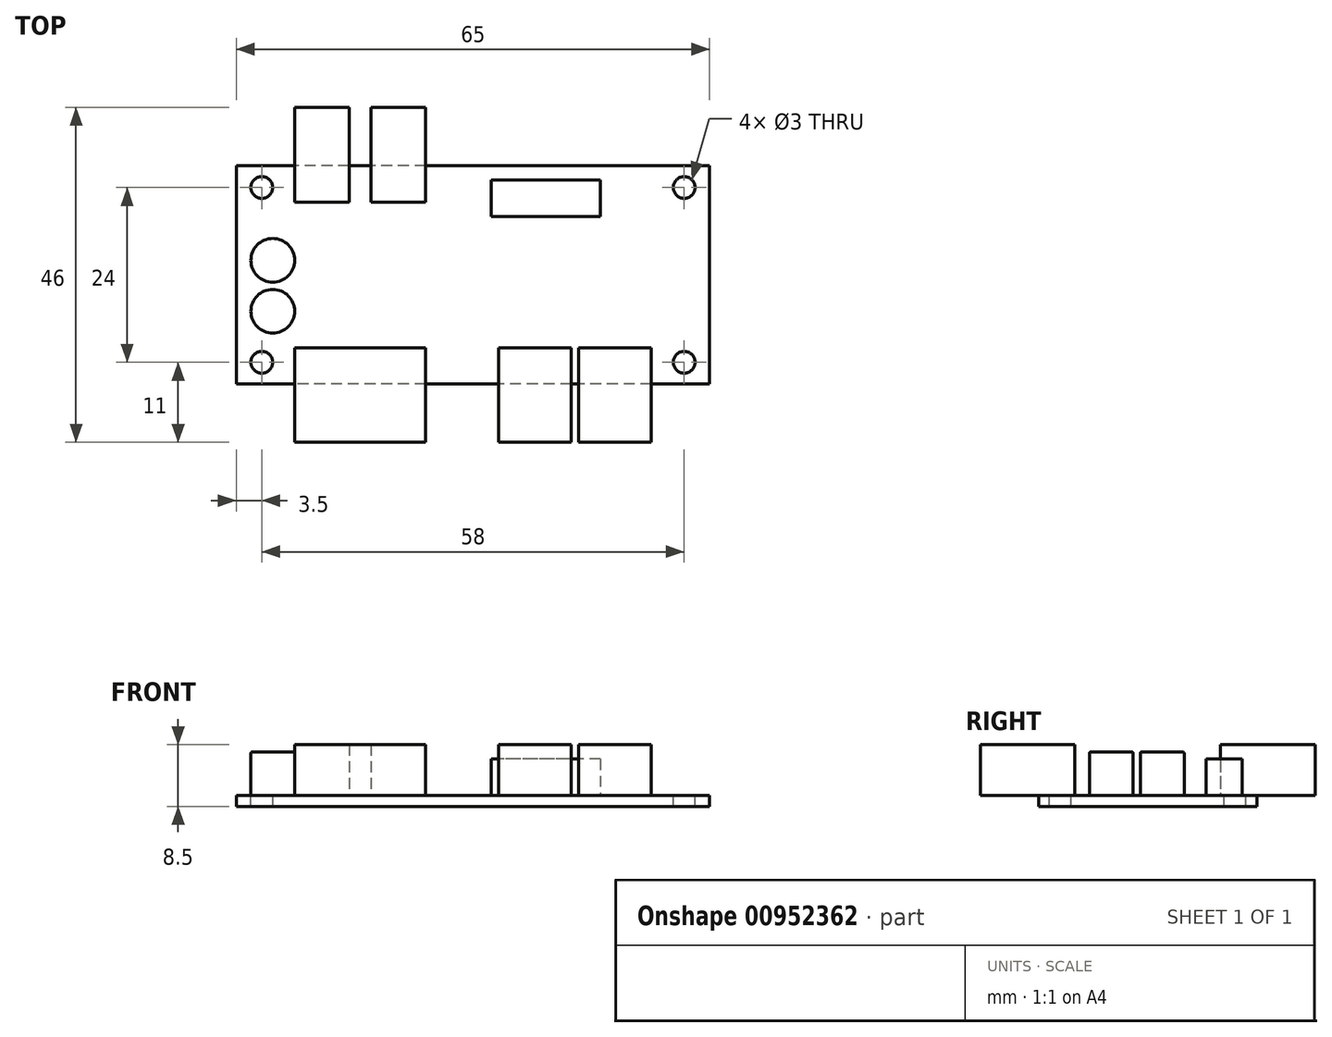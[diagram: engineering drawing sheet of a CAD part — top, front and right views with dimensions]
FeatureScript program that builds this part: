
annotation { "Feature Type Name" : "Feature", "Feature Type Description" : "" }
export const myFeature = defineFeature(function(context is Context, id is Id, definition is map)
    precondition{}
    {
        {
            var Q0;
            Q0=qCreatedBy(makeId("Top.planeOp"),FACE);
            var sketch = newSketch(context, id + "F0", { "sketchPlane" : qUnion([Q0])});
            skLineSegment(sketch, "E0.bottom", {"start": v(32.5, 15) * mm, "end": v(-32.5, 15) * mm});
            skLineSegment(sketch, "E0.top", {"start": v(32.5, -15) * mm, "end": v(-32.5, -15) * mm});
            skLineSegment(sketch, "E0.left", {"start": v(32.5, 15) * mm, "end": v(32.5, -15) * mm});
            skLineSegment(sketch, "E0.right", {"start": v(-32.5, 15) * mm, "end": v(-32.5, -15) * mm});
            skPoint(sketch, "E0.middle", {"position": v(0, 0) * mm});
            skSolve(sketch);
        }
        {
            var Q0;
            Q0 = qSketchRegion(id + "F0", true);
            extrude(context, id + "F1", {"entities" : qUnion([Q0]), "depth" : 1.5 * mm, "offsetDistance" : 25 * mm});
        }
        {
            var Q0;
            Q0=makeQuery(id+"F1.opExtrude","CAP_FACE",FACE,{"disambiguationData":[OSD([sQuery(id+"F0.wireOp",EDGE,"E0.bottom"),sQuery(id+"F0.wireOp",EDGE,"E0.top"),sQuery(id+"F0.wireOp",EDGE,"E0.left"),sQuery(id+"F0.wireOp",EDGE,"E0.right")])],"isStart":false});
            var sketch = newSketch(context, id + "F2", { "sketchPlane" : qUnion([Q0])});
            skCircle(sketch, "E1", {"center": v(-29, 12) * mm, "radius": 1.5 * mm});
            skCircle(sketch, "E2.0.1.0", {"center": v(-29, -12) * mm, "radius": 1.5 * mm});
            skCircle(sketch, "E2.1.0.0", {"center": v(29, 12) * mm, "radius": 1.5 * mm});
            skCircle(sketch, "E2.1.1.0", {"center": v(29, -12) * mm, "radius": 1.5 * mm});
            skLineSegment(sketch, "E2.direction1", {"start": v(-29, 12) * mm, "end": v(29, 12) * mm, "construction": true});
            skLineSegment(sketch, "E2.direction2", {"start": v(-29, 12) * mm, "end": v(-29, -12) * mm, "construction": true});
            skSolve(sketch);
        }
        {
            var Q0;
            Q0 = qSketchRegion(id + "F2", true);
            extrude(context, id + "F3", {"entities" : qUnion([Q0]), "operationType" : NewBodyOperationType.REMOVE, "endBound" : BoundingType.THROUGH_ALL, "oppositeDirection" : true, "depth" : 25 * mm, "offsetDistance" : 25 * mm});
        }
        {
            var Q0;
            Q0=makeQuery(id+"F1.opExtrude","CAP_FACE",FACE,{"disambiguationData":[OSD([sQuery(id+"F0.wireOp",EDGE,"E0.bottom"),sQuery(id+"F0.wireOp",EDGE,"E0.top"),sQuery(id+"F0.wireOp",EDGE,"E0.left"),sQuery(id+"F0.wireOp",EDGE,"E0.right")])],"isStart":false});
            var sketch = newSketch(context, id + "F4", { "sketchPlane" : qUnion([Q0])});
            skCircle(sketch, "E3", {"center": v(-27.5, 2) * mm, "radius": 3 * mm});
            skCircle(sketch, "E4", {"center": v(-27.5, -5) * mm, "radius": 3 * mm});
            skSolve(sketch);
        }
        {
            var Q0;
            Q0 = qSketchRegion(id + "F4", true);
            extrude(context, id + "F5", {"entities" : qUnion([Q0]), "operationType" : NewBodyOperationType.ADD, "depth" : 6 * mm, "offsetDistance" : 25 * mm});
        }
        {
            var Q0;
            Q0=makeQuery(id+"F5.opExtrude","CAP_EDGE",EDGE,{"disambiguationData":[OSD([sQuery(id+"F4.wireOp",EDGE,"E3")])],"isStart":false});
            var Q1;
            Q1=makeQuery(id+"F5.opExtrude","CAP_EDGE",EDGE,{"disambiguationData":[OSD([sQuery(id+"F4.wireOp",EDGE,"E4")])],"isStart":false});
            fillet(context, id + "F6", {"entities" : qUnion([Q0, Q1]), "radius" : 0.2 * mm, "tangentPropagation" : true, "allowEdgeOverflow" : false});
        }
        {
            var Q0;
            Q0=makeQuery(id+"F1.opExtrude","CAP_FACE",FACE,{"disambiguationData":[OSD([sQuery(id+"F0.wireOp",EDGE,"E0.bottom"),sQuery(id+"F0.wireOp",EDGE,"E0.top"),sQuery(id+"F0.wireOp",EDGE,"E0.left"),sQuery(id+"F0.wireOp",EDGE,"E0.right")])],"isStart":false});
            var sketch = newSketch(context, id + "F7", { "sketchPlane" : qUnion([Q0])});
            skLineSegment(sketch, "E5.bottom", {"start": v(-17, 23) * mm, "end": v(-24.5, 23) * mm});
            skLineSegment(sketch, "E5.top", {"start": v(-17, 10) * mm, "end": v(-24.5, 10) * mm});
            skLineSegment(sketch, "E5.left", {"start": v(-17, 23) * mm, "end": v(-17, 10) * mm});
            skLineSegment(sketch, "E5.right", {"start": v(-24.5, 23) * mm, "end": v(-24.5, 10) * mm});
            skPoint(sketch, "E5.middle", {"position": v(-20.75, 16.5) * mm});
            skLineSegment(sketch, "E6.1.0.0", {"start": v(-6.5, 10) * mm, "end": v(-14, 10) * mm});
            skLineSegment(sketch, "E6.1.0.1", {"start": v(-14, 23) * mm, "end": v(-14, 10) * mm});
            skLineSegment(sketch, "E6.1.0.2", {"start": v(-6.5, 23) * mm, "end": v(-6.5, 10) * mm});
            skPoint(sketch, "E6.1.0.3", {"position": v(-10.25, 16.5) * mm});
            skLineSegment(sketch, "E6.1.0.4", {"start": v(-6.5, 23) * mm, "end": v(-14, 23) * mm});
            skLineSegment(sketch, "E6.direction1", {"start": v(-24.5, 10) * mm, "end": v(-14, 10) * mm, "construction": true});
            skLineSegment(sketch, "E7.bottom", {"start": v(-6.5, -23) * mm, "end": v(-24.5, -23) * mm});
            skLineSegment(sketch, "E7.top", {"start": v(-6.5, -10) * mm, "end": v(-24.5, -10) * mm});
            skLineSegment(sketch, "E7.left", {"start": v(-6.5, -23) * mm, "end": v(-6.5, -10) * mm});
            skLineSegment(sketch, "E7.right", {"start": v(-24.5, -23) * mm, "end": v(-24.5, -10) * mm});
            skPoint(sketch, "E7.middle", {"position": v(-15.5, -16.5) * mm});
            skLineSegment(sketch, "E8.bottom", {"start": v(24.5, -10) * mm, "end": v(14.5, -10) * mm});
            skLineSegment(sketch, "E8.top", {"start": v(24.5, -23) * mm, "end": v(14.5, -23) * mm});
            skLineSegment(sketch, "E8.left", {"start": v(24.5, -10) * mm, "end": v(24.5, -23) * mm});
            skLineSegment(sketch, "E8.right", {"start": v(14.5, -10) * mm, "end": v(14.5, -23) * mm});
            skPoint(sketch, "E8.middle", {"position": v(19.5, -16.5) * mm});
            skLineSegment(sketch, "E9.1.0.0", {"start": v(13.5, -10) * mm, "end": v(3.5, -10) * mm});
            skPoint(sketch, "E9.1.0.1", {"position": v(8.5, -16.5) * mm});
            skLineSegment(sketch, "E9.1.0.2", {"start": v(13.5, -10) * mm, "end": v(13.5, -23) * mm});
            skLineSegment(sketch, "E9.1.0.3", {"start": v(3.5, -10) * mm, "end": v(3.5, -23) * mm});
            skLineSegment(sketch, "E9.1.0.4", {"start": v(13.5, -23) * mm, "end": v(3.5, -23) * mm});
            skLineSegment(sketch, "E9.direction1", {"start": v(14.5, -23) * mm, "end": v(3.5, -23) * mm, "construction": true});
            skSolve(sketch);
        }
        {
            var Q0;
            Q0 = qSketchRegion(id + "F7", true);
            extrude(context, id + "F8", {"entities" : qUnion([Q0]), "operationType" : NewBodyOperationType.ADD, "depth" : 7 * mm, "offsetDistance" : 25 * mm});
        }
        {
            var Q0;
            Q0=makeQuery(id+"F1.opExtrude","CAP_FACE",FACE,{"disambiguationData":[OSD([sQuery(id+"F0.wireOp",EDGE,"E0.bottom"),sQuery(id+"F0.wireOp",EDGE,"E0.top"),sQuery(id+"F0.wireOp",EDGE,"E0.left"),sQuery(id+"F0.wireOp",EDGE,"E0.right")])],"isStart":false});
            var sketch = newSketch(context, id + "F9", { "sketchPlane" : qUnion([Q0])});
            skLineSegment(sketch, "E10.bottom", {"start": v(17.5, 13) * mm, "end": v(2.5, 13) * mm});
            skLineSegment(sketch, "E10.top", {"start": v(17.5, 8) * mm, "end": v(2.5, 8) * mm});
            skLineSegment(sketch, "E10.left", {"start": v(17.5, 13) * mm, "end": v(17.5, 8) * mm});
            skLineSegment(sketch, "E10.right", {"start": v(2.5, 13) * mm, "end": v(2.5, 8) * mm});
            skPoint(sketch, "E10.middle", {"position": v(10, 10.5) * mm});
            skSolve(sketch);
        }
        {
            var Q0;
            Q0 = qSketchRegion(id + "F9", true);
            extrude(context, id + "F10", {"entities" : qUnion([Q0]), "operationType" : NewBodyOperationType.ADD, "depth" : 5 * mm, "offsetDistance" : 25 * mm});
        }
    });
